# Revit family: Domotics-DomesticRanges-GEWISS-CHORUS_POWER-SOCKET-OUTLET_ITA_2xP11P17_16A
name_source: partatom
category: Apparecchi elettrici
revit_build: Autodesk Revit 2016 (Build: 20161004_0715(x64)
units: mm (PartAtom-declared; Revit-internal decimal feet)

## family parameters
Condiviso = Sì
Host = Superficie
Mantenere orientamento annotazione = Sì
Numero OmniClass = 23.80.50.14
Punto di calcolo locali = No
Quota connettore circolare = Usa diametro
Taglio con vuoti quando caricato = Sì
Tipo di parte = Normale
Titolo OmniClass = Plug Connectors

## types (3) — shared parameters
Breaking capacity: = 1.25 In (100 position changes)
Catalogue = DOMOTICS
Catalogue Range = CHORUS - DOMESTIC RANGE
Category = Double socket-outlet
Characteristics = With safety shields
Description. = Double socket-outlet
Description: = 2x2P+E - 16A Dual amperage
Electrocod = 0131
For plug pins = Ã˜ 4 / 5 mm
Glow Wire Test = 850°C
IDF = 0beabf91-52fa-4b9d-8450-2fb65aae4f08
IDT = 0d330754-0b03-49b4-9722-6411f775bea8
Immagine tipo = GW14208.jpg
Insulation resistance = > 5 MOhm
Larghezza presa = 46 mm  [stored 0.150919 ft]
No. Chorus modules = 2
No. Chorus modules: = 2
Produttore = GEWISS S.p.A.
Prolonged operation (no.of position changes) = 10.000 at In 250 V ac cosÃ˜=0,8
Prospetto di default = 1219 mm
Resistance at test voltage = 2000 V at 50 Hz for 1 minute
SEO = Socket outlet
Simbolo = SIMBOLO PRESE DOPPIE : PRESA DOPPIA
Socket-out type = P11-P17
Standard = English
Standard: = English
Standard; = IEC 60884-1
Technical sheet = https://www.gewiss.com
Terminal grip on cable traction = > 50 N
Terminal tightening capacity flexible cables (mm2) = min. 0,75 - max. 2x4
Terminal tightening capacity rigid cables (mm2) = min. 0,5 - max. 2x2,5
Thermo-pressure with ball = 125
Tipo = CHORUS PRESE DOPPIE ITA P11-17 16A_BASE : GW14906 - Titanio
URL = https://www.gewiss.com
Version file RFA = 19.0
Voltage = 250 V ac
Voltage: = 250 V ac
Wiring terminals = With screw

## per-type parameters (varying)
| type | Colour | Descrizione | EAN code | Modello |
| GW12208 - Black | Black | DBL SOC, 2P+E 16A P17-11 D.AM IT/G ST B | 8011564269507 | GW12208 |
| GW10208 - White | White | 2XS. OUT. 2P+E 16A P17-11 D.AM IT WH | 8011564258655 | GW10208 |
| GW14208 - Titanium | Titanium | DBL SOCKET 2P+E 16A P17-11 D.AM IT ST T | 8011564266339 | GW14208 |

note: source unit labels omitted for Thermo-pressure with ball — the stored unit's dimension contradicts the parameter name (converter mislabeling)

note: [stored X ft] marks values corroborated as IEEE doubles in the binary element streams (Revit-internal decimal feet)

## geometry (parser evidence)
native form markers: Sweep x1
no freeform markers — native parametric forms only
